# Revit family: 54e35ebe_eb28_45ad_82de_a73b42f401df
name_source: partatom
category: Generic Models
revit_build: Autodesk Revit Architecture 2015 (Build: 20140606_1530(x64)
units: mm (PartAtom-declared; Revit-internal decimal feet)

## types (1)
- Default
    BIMobject category = Office Furniture
    BOSUseNativeGeometries = 0
    Design country = Spain
    Edition number = 1
    IFC Classification = Furniture
    Manufacturer country = Spain
    Manufacturer name = Actiu
    Material main = Melamine
    Material secondary = Aluminium
    NBS Reference Code = 35-12-58
    NBS Reference Description = Office Desks
    Nominal height = 740
    Nominal width = 800
    OmniClass Code = 23-21 13 25
    OmniClass Description = Office Equipment
    Product Guid = 95d97aa2-bc69-4ba9-a851-28ea6477917c
    Product SKU = mobilityprofixedtraining
    Product certification = http://www.actiu.com
    Product data url = https://bimobject.com
    Product family = Mobility
    Product group = Mobility Pro
    Product name = Mobility Pro_Fixed Desks_Training
    QR code = http://bimobject.com
    Technical description = http://www.actiu.com
    UNSPSC Code = 44
    Uniclass 1.4 Code = L853
    Uniclass 1.4 Description = Office furniture
    Uniclass 2.0 Code = PR-35-12-58
    Uniclass 2.0 Description = Office Desks
    Uniclass 2015 Code = Pr_40_50_21_59
    Uniclass 2015 Name = Office desks
    Weight Net (Kg) = 0
    Youtube clip = https://www.youtube.com

## geometry (parser evidence)
native form markers: Sweep x2
no freeform markers — native parametric forms only
